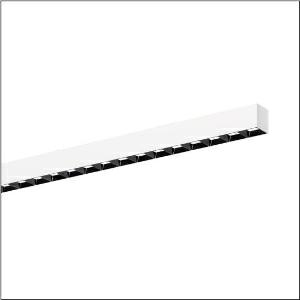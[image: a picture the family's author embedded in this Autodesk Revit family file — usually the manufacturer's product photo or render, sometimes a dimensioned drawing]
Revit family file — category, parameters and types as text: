
# Revit family: silica_r__21_51mx24dc4awb_a921
name_source: partatom
category: Lighting Fixtures
units: mm (PartAtom-declared; Revit-internal decimal feet)

## family parameters
Cut with Voids When Loaded = No
Host = Face
Light Source = No
Part Type = Normal
Room Calculation Point = No
Round Connector Dimension = Use Diameter
Shared = No

## types (1)
- --- (1 x LED, 10800 lm, 73.7 W, 4000K)
    Apparent Load = 74 VA
    CIE Flux Codes = 74 94 99 100 100
    Color Rendering = 80
    Color Temperature = 4000K
    Default Elevation = 1800 mm
    Description = Silica® 21, office luminaire, primary light control with darklight reflector, of PMMA, black, CAT 2 (L<= 3000cd/m²), light emission: direct distribution, primary light characteristic: asymmetric, installation type: surface-mounted, LED, rated luminous flux: 10.800lm, luminous efficacy: 147lm/W, light colour: 840, colour temperature: 4000K, with terminal, 3+2-pole, max. 2.5mm², mains connection: 220..240V, AC, 50/60Hz, rated input power: 73.7W, luminaire housing, of aluminium, traffic white (RAL 9016), length: 3.004mm, width: 53mm, height: 53mm, protection rating (complete): IP20, insulation class (complete): insulation class I (protective earthing), certification: CE, permissible operating ambient temperature: 0..+35°C, standard: EN 50419, packaging unit: 1 piece
    Height = 0 mm  [stored 0 ft]
    Lamp = 1 x LED
    Lamp Light Flux = 10800 lm
    Lamp Power = 73.7 W
    Lamp count = 1
    Length = 3004 mm
    Luminous efficacy = 147 lm/W
    Manufacturer = Siteco
    ModVariant = No
    Model = 51MX24DC4AWB
    Mounting Place = Ceiling
    Mounting Type = Recessed
    Number of Poles = 1
    OnlyDefault = Yes
    Power Factor = 1
    Product Name = Silica® 21
    Product group = office luminaire | ceiling recessed
    ProductGroupID = 401
    Protection Class = Protection class I
    Protection Degree = IP 20
    RLX_Detail_Level = 1
    RLX_Emergency_Light_Flux = 0 lm
    RLX_Emergency_Type = 0
    RLX_Emergency_Type_DB = No
    RlxData = <blob elided: 64065 chars, md5=0051bd27>
    Socket = socket
    Standby Power = 0 W
    System Light Flux = 10800 lm
    System Power = 74 W
    Type Comments = factory setting: luminous flux: 100 % | dim-lin: 254 | 418 mA
    Type Image = l_1313592.jpg
    URL = http://relux.com
    VarID = @adj_071971
    Voltage = 0 V
    Weight = 0.00 kg
    Width = 53 mm

note: [stored X ft] marks values corroborated as IEEE doubles in the binary element streams (Revit-internal decimal feet)

## geometry (parser evidence)
native form markers: Blend x4, Sweep x8
no freeform markers — native parametric forms only
